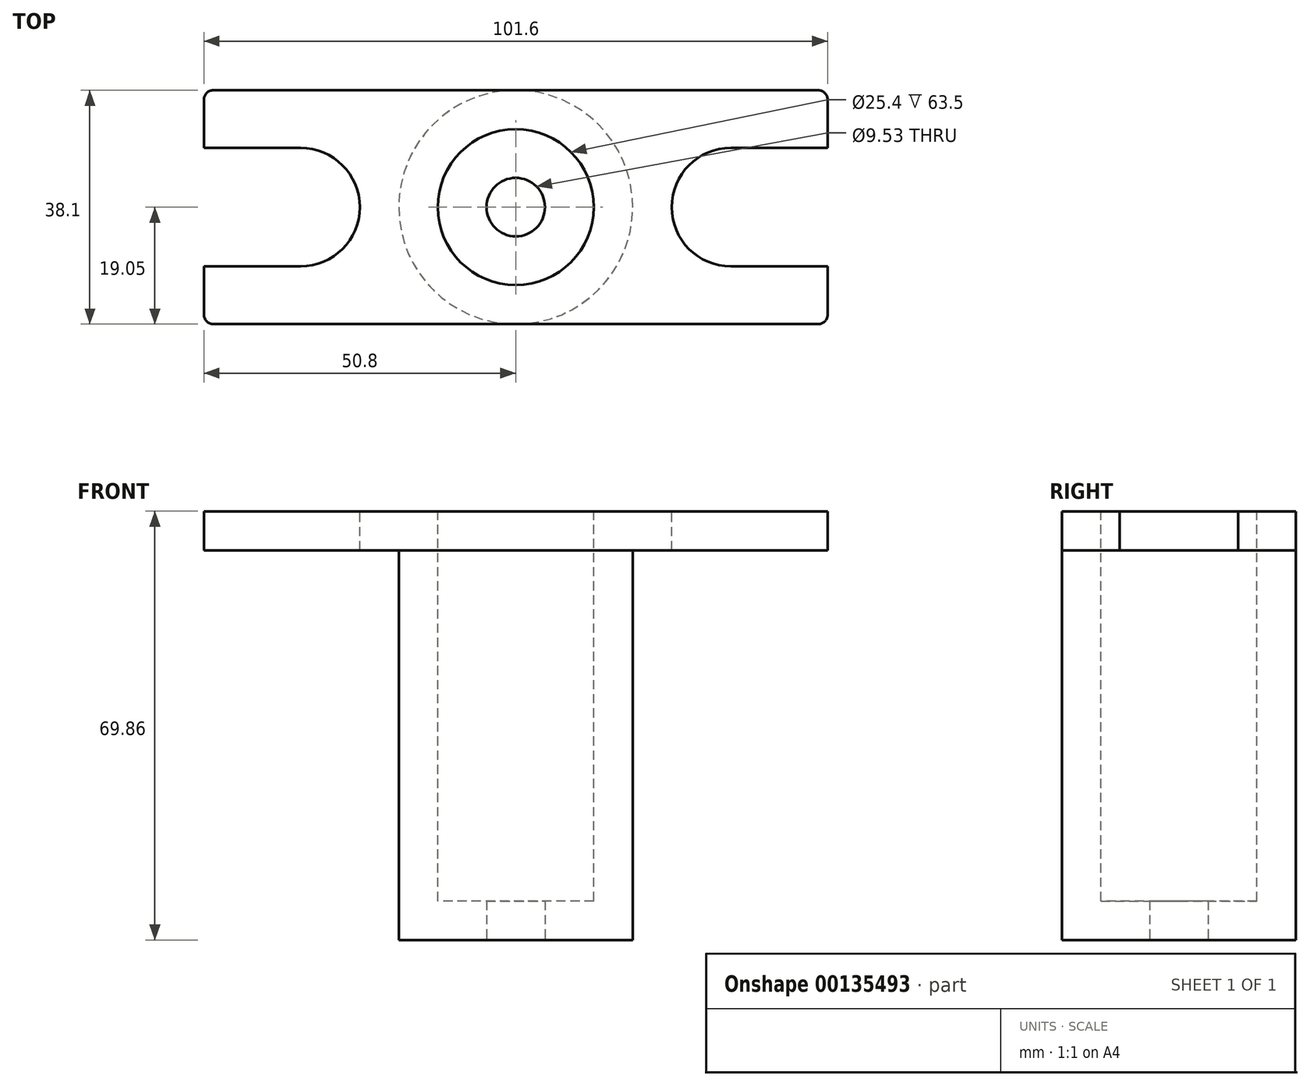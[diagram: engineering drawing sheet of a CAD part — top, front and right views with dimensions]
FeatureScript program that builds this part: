
annotation { "Feature Type Name" : "Feature", "Feature Type Description" : "" }
export const myFeature = defineFeature(function(context is Context, id is Id, definition is map)
    precondition{}
    {
        {
            var Q0;
            Q0=qCreatedBy(makeId("Front.planeOp"),FACE);
            var sketch = newSketch(context, id + "F0", { "sketchPlane" : qUnion([Q0])});
            skLineSegment(sketch, "E0.bottom", {"start": v(-50.8, 3.17) * mm, "end": v(50.8, 3.18) * mm});
            skLineSegment(sketch, "E0.top", {"start": v(-50.8, -3.18) * mm, "end": v(50.8, -3.17) * mm});
            skLineSegment(sketch, "E0.left", {"start": v(-50.8, 3.17) * mm, "end": v(-50.8, -3.18) * mm});
            skLineSegment(sketch, "E0.right", {"start": v(50.8, 3.18) * mm, "end": v(50.8, -3.17) * mm});
            skSolve(sketch);
        }
        {
            var Q0;
            Q0 = qSketchRegion(id + "F0", true);
            extrude(context, id + "F1", {"entities" : qUnion([Q0]), "endBound" : BoundingType.SYMMETRIC, "depth" : 38.1 * mm});
        }
        {
            var Q0;
            Q0=makeQuery(id+"F1.opExtrude","SWEPT_FACE",FACE,{"disambiguationData":[OSD([sQuery(id+"F0.wireOp",EDGE,"E0.bottom")])]});
            var sketch = newSketch(context, id + "F2", { "sketchPlane" : qUnion([Q0])});
            skCircle(sketch, "E1", {"center": v(0, 0) * mm, "radius": 19.05 * mm});
            skSolve(sketch);
        }
        {
            var Q0;
            Q0 = qSketchRegion(id + "F2", true);
            extrude(context, id + "F3", {"entities" : qUnion([Q0]), "operationType" : NewBodyOperationType.ADD, "oppositeDirection" : true, "depth" : 69.85 * mm});
        }
        {
            var Q0;
            Q0=makeQuery(id+"F1.opExtrude","SWEPT_FACE",FACE,{"disambiguationData":[OSD([sQuery(id+"F0.wireOp",EDGE,"E0.bottom")])]});
            var sketch = newSketch(context, id + "F4", { "sketchPlane" : qUnion([Q0])});
            skCircle(sketch, "E2", {"center": v(0, 0) * mm, "radius": 12.7 * mm});
            skSolve(sketch);
        }
        {
            var Q0;
            Q0 = qSketchRegion(id + "F4", true);
            extrude(context, id + "F5", {"entities" : qUnion([Q0]), "operationType" : NewBodyOperationType.REMOVE, "oppositeDirection" : true, "depth" : 63.5 * mm});
        }
        {
            var Q0;
            Q0=makeQuery(id+"F3.opExtrude","CAP_FACE",FACE,{"disambiguationData":[OSD([sQuery(id+"F2.wireOp",EDGE,"E1")])],"isStart":false});
            var sketch = newSketch(context, id + "F6", { "sketchPlane" : qUnion([Q0])});
            skCircle(sketch, "E3", {"center": v(0, 0) * mm, "radius": 4.76 * mm});
            skSolve(sketch);
        }
        {
            var Q0;
            Q0 = qSketchRegion(id + "F6", true);
            extrude(context, id + "F7", {"entities" : qUnion([Q0]), "operationType" : NewBodyOperationType.REMOVE, "oppositeDirection" : true, "depth" : 6.35 * mm});
        }
        {
            var Q0;
            Q0=makeQuery(id+"F1.opExtrude","SWEPT_FACE",FACE,{"disambiguationData":[OSD([sQuery(id+"F0.wireOp",EDGE,"E0.bottom")])]});
            var sketch = newSketch(context, id + "F8", { "sketchPlane" : qUnion([Q0])});
            skLineSegment(sketch, "E4", {"start": v(50.8, 9.65) * mm, "end": v(35.05, 9.65) * mm});
            skLineSegment(sketch, "E5", {"start": v(50.8, -9.65) * mm, "end": v(35.05, -9.65) * mm});
            skArc(sketch, "E6", {"start": v(35.05, 9.65) * mm, "mid": v(25.4, 0) * mm, "end": v(35.05, -9.65) * mm});
            skLineSegment(sketch, "E7", {"start": v(50.8, 9.65) * mm, "end": v(50.8, -9.65) * mm});
            skSolve(sketch);
        }
        {
            var Q0;
            Q0 = qSketchRegion(id + "F8", true);
            extrude(context, id + "F9", {"entities" : qUnion([Q0]), "operationType" : NewBodyOperationType.REMOVE, "oppositeDirection" : true, "depth" : 25.4 * mm});
        }
        {
            var Q0;
            Q0=makeQuery(id+"F1.opExtrude","SWEPT_FACE",FACE,{"disambiguationData":[OSD([sQuery(id+"F0.wireOp",EDGE,"E0.bottom")])]});
            var sketch = newSketch(context, id + "F10", { "sketchPlane" : qUnion([Q0])});
            skLineSegment(sketch, "E8", {"start": v(-50.8, 9.65) * mm, "end": v(-35.05, 9.65) * mm});
            skLineSegment(sketch, "E9", {"start": v(-50.8, -9.65) * mm, "end": v(-35.05, -9.65) * mm});
            skArc(sketch, "E10", {"start": v(-35.05, -9.65) * mm, "mid": v(-25.4, 0) * mm, "end": v(-35.05, 9.65) * mm});
            skLineSegment(sketch, "E11", {"start": v(-50.8, 9.65) * mm, "end": v(-50.8, -9.65) * mm});
            skSolve(sketch);
        }
        {
            var Q0;
            Q0 = qSketchRegion(id + "F10", true);
            extrude(context, id + "F11", {"entities" : qUnion([Q0]), "operationType" : NewBodyOperationType.REMOVE, "oppositeDirection" : true, "depth" : 25.4 * mm});
        }
        {
            var Q0;
            Q0=makeQuery(id+"F1.opExtrude","CAP_EDGE",EDGE,{"disambiguationData":[OSD([sQuery(id+"F0.wireOp",EDGE,"E0.right")])],"isStart":false});
            var Q1;
            Q1=makeQuery(id+"F1.opExtrude","CAP_EDGE",EDGE,{"disambiguationData":[OSD([sQuery(id+"F0.wireOp",EDGE,"E0.right")])],"isStart":true});
            var Q2;
            Q2=makeQuery(id+"F1.opExtrude","CAP_EDGE",EDGE,{"disambiguationData":[OSD([sQuery(id+"F0.wireOp",EDGE,"E0.left")])],"isStart":false});
            var Q3;
            Q3=makeQuery(id+"F1.opExtrude","CAP_EDGE",EDGE,{"disambiguationData":[OSD([sQuery(id+"F0.wireOp",EDGE,"E0.left")])],"isStart":true});
            fillet(context, id + "F12", {"entities" : qUnion([Q0, Q1, Q2, Q3]), "radius" : 1.52 * mm, "tangentPropagation" : true, "allowEdgeOverflow" : false});
        }
    });
